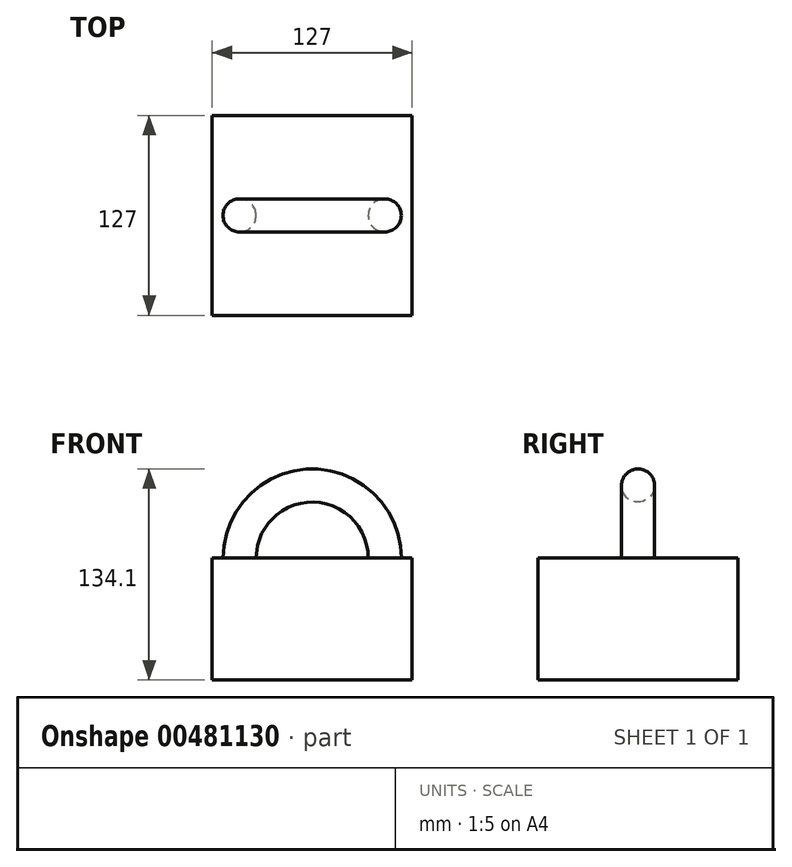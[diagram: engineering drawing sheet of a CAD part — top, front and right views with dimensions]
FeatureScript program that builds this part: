
annotation { "Feature Type Name" : "Feature", "Feature Type Description" : "" }
export const myFeature = defineFeature(function(context is Context, id is Id, definition is map)
    precondition{}
    {
        {
            var Q0;
            Q0=qCreatedBy(makeId("Top.planeOp"),FACE);
            var sketch = newSketch(context, id + "F0", { "sketchPlane" : qUnion([Q0])});
            skLineSegment(sketch, "E0.bottom", {"start": v(63.5, -63.5) * mm, "end": v(-63.5, -63.5) * mm});
            skLineSegment(sketch, "E0.top", {"start": v(63.5, 63.5) * mm, "end": v(-63.5, 63.5) * mm});
            skLineSegment(sketch, "E0.left", {"start": v(63.5, -63.5) * mm, "end": v(63.5, 63.5) * mm});
            skLineSegment(sketch, "E0.right", {"start": v(-63.5, -63.5) * mm, "end": v(-63.5, 63.5) * mm});
            skPoint(sketch, "E0.middle", {"position": v(0, 0) * mm});
            skLineSegment(sketch, "E1", {"start": v(0, 63.5) * mm, "end": v(0, -63.5) * mm});
            skSolve(sketch);
        }
        {
            var Q0;
            Q0=qCreatedBy(makeId("Top.planeOp"),FACE);
            var sketch = newSketch(context, id + "F1", { "sketchPlane" : qUnion([Q0])});
            skCircle(sketch, "E2", {"center": v(46.11, 0) * mm, "radius": 10.52 * mm});
            skSolve(sketch);
        }
        {
            var Q0;
            {var subQ0=sQuery(id+"F0.wireOp",EDGE,"E0.right");Q0=makeQuery(id+"F0.imprint","IMPRINT",FACE,{"disambiguationData":[TD([[makeQuery(id+"F0.imprint","IMPRINT",EDGE,{"derivedFrom":subQ0}),-1.0]])]});}
            var Q1;
            {var subQ0=sQuery(id+"F0.wireOp",EDGE,"E0.left");Q1=makeQuery(id+"F0.imprint","IMPRINT",FACE,{"disambiguationData":[TD([[makeQuery(id+"F0.imprint","IMPRINT",EDGE,{"derivedFrom":subQ0}),1.0]])]});}
            extrude(context, id + "F2", {"entities" : qUnion([Q0, Q1]), "oppositeDirection" : true, "depth" : 77.47 * mm});
        }
        {
            var Q0;
            Q0 = qSketchRegion(id + "F1", true);
            var Q1;
            Q1=sQuery(id+"F0.wireOp",EDGE,"E1");
            revolve(context, id + "F3", {"operationType" : NewBodyOperationType.ADD, "entities" : qUnion([Q0]), "axis" : qUnion([Q1]), "revolveType" : RevolveType.FULL});
        }
    });
